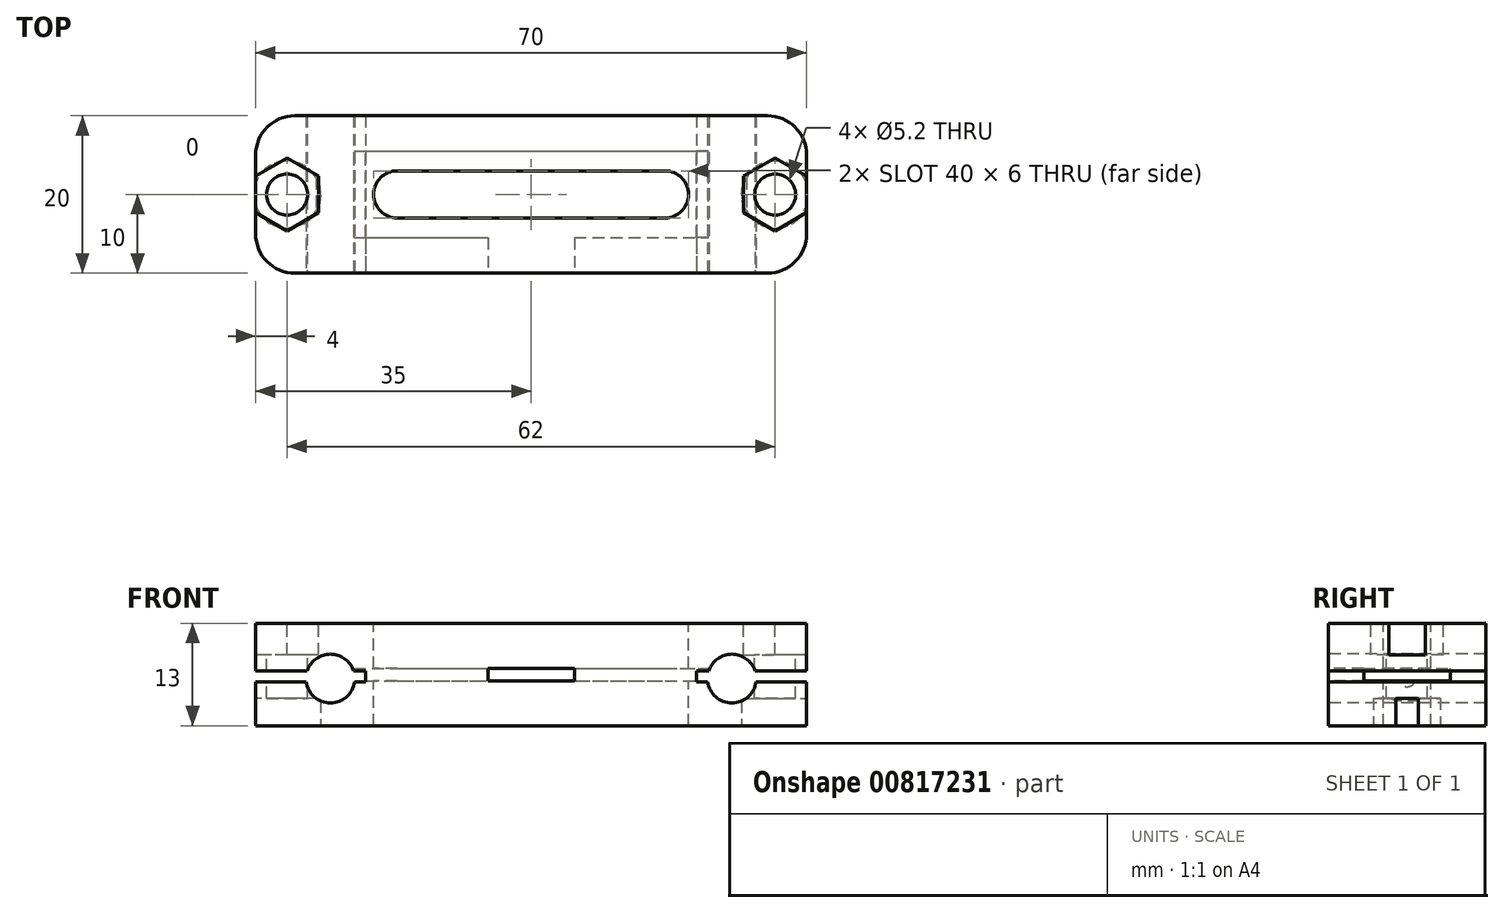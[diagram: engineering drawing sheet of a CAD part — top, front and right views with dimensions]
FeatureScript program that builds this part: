
annotation { "Feature Type Name" : "Feature", "Feature Type Description" : "" }
export const myFeature = defineFeature(function(context is Context, id is Id, definition is map)
    precondition{}
    {
        {
            var Q0;
            Q0=qCreatedBy(makeId("Top.planeOp"),FACE);
            var sketch = newSketch(context, id + "F0", { "sketchPlane" : qUnion([Q0])});
            skLineSegment(sketch, "E0.bottom", {"start": v(35, -10) * mm, "end": v(-35, -10) * mm});
            skLineSegment(sketch, "E0.top", {"start": v(35, 10) * mm, "end": v(-35, 10) * mm});
            skLineSegment(sketch, "E0.left", {"start": v(35, -10) * mm, "end": v(35, 10) * mm});
            skLineSegment(sketch, "E0.right", {"start": v(-35, -10) * mm, "end": v(-35, 10) * mm});
            skPoint(sketch, "E0.middle", {"position": v(0, 0) * mm});
            skSolve(sketch);
        }
        {
            var Q0;
            Q0 = qSketchRegion(id + "F0", true);
            extrude(context, id + "F1", {"entities" : qUnion([Q0]), "endBound" : BoundingType.SYMMETRIC, "depth" : 13 * mm, "offsetDistance" : 25 * mm});
        }
        {
            var Q0;
            Q0=makeQuery(id+"F1.opExtrude","CAP_FACE",FACE,{"disambiguationData":[OSD([sQuery(id+"F0.wireOp",EDGE,"E0.bottom"),sQuery(id+"F0.wireOp",EDGE,"E0.top"),sQuery(id+"F0.wireOp",EDGE,"E0.left"),sQuery(id+"F0.wireOp",EDGE,"E0.right")])],"isStart":false});
            var sketch = newSketch(context, id + "F2", { "sketchPlane" : qUnion([Q0])});
            skLineSegment(sketch, "E1.bottom", {"start": v(17, -3) * mm, "end": v(-17, -3) * mm});
            skLineSegment(sketch, "E1.top", {"start": v(17, 3) * mm, "end": v(-17, 3) * mm});
            skPoint(sketch, "E1.middle", {"position": v(0, 0) * mm});
            skArc(sketch, "E2", {"start": v(-17, 3) * mm, "mid": v(-20, 0) * mm, "end": v(-17, -3) * mm});
            skArc(sketch, "E3", {"start": v(17, 3) * mm, "mid": v(20, 0) * mm, "end": v(17, -3) * mm});
            skSolve(sketch);
        }
        {
            var Q0;
            Q0=makeQuery(id+"F2.imprint","IMPRINT",FACE,{"disambiguationData":[TD([[makeQuery(id+"F2.imprint","IMPRINT",EDGE,{"derivedFrom":sQuery(id+"F2.wireOp",EDGE,"E1.bottom")}),1.0]])]});
            var sketch = newSketch(context, id + "F3", { "sketchPlane" : qUnion([Q0])});
            skCircle(sketch, "E4.cCircle", {"center": v(-31, 0) * mm, "radius": 4 * mm, "construction": true});
            skLineSegment(sketch, "E4.0", {"start": v(-27, -2.3) * mm, "end": v(-31, -4.62) * mm});
            skLineSegment(sketch, "E4.1", {"start": v(-31, -4.62) * mm, "end": v(-35, -2.3) * mm});
            skLineSegment(sketch, "E4.2", {"start": v(-35, -2.3) * mm, "end": v(-35, 2.3) * mm});
            skLineSegment(sketch, "E4.3", {"start": v(-35, 2.3) * mm, "end": v(-31, 4.62) * mm});
            skLineSegment(sketch, "E4.4", {"start": v(-31, 4.62) * mm, "end": v(-27, 2.3) * mm});
            skLineSegment(sketch, "E4.5", {"start": v(-27, 2.3) * mm, "end": v(-27, -2.3) * mm});
            skPoint(sketch, "E4.0.midPoint", {"position": v(-29, -3.46) * mm});
            skCircle(sketch, "E5.cCircle", {"center": v(31, 0) * mm, "radius": 4 * mm, "construction": true});
            skLineSegment(sketch, "E5.0", {"start": v(35, 2.3) * mm, "end": v(35, -2.3) * mm});
            skLineSegment(sketch, "E5.1", {"start": v(35, -2.3) * mm, "end": v(31, -4.62) * mm});
            skLineSegment(sketch, "E5.2", {"start": v(31, -4.62) * mm, "end": v(27, -2.3) * mm});
            skLineSegment(sketch, "E5.3", {"start": v(27, -2.3) * mm, "end": v(27, 2.3) * mm});
            skLineSegment(sketch, "E5.4", {"start": v(27, 2.3) * mm, "end": v(31, 4.62) * mm});
            skLineSegment(sketch, "E5.5", {"start": v(31, 4.62) * mm, "end": v(35, 2.3) * mm});
            skPoint(sketch, "E5.0.midPoint", {"position": v(35, 0) * mm});
            skSolve(sketch);
        }
        {
            var Q0;
            Q0 = qSketchRegion(id + "F3", true);
            extrude(context, id + "F4", {"entities" : qUnion([Q0]), "operationType" : NewBodyOperationType.REMOVE, "oppositeDirection" : true, "depth" : 4 * mm, "offsetDistance" : 25 * mm});
        }
        {
            var Q0;
            Q0=makeQuery(id+"F2.imprint","IMPRINT",FACE,{"disambiguationData":[TD([[makeQuery(id+"F2.imprint","IMPRINT",EDGE,{"derivedFrom":sQuery(id+"F2.wireOp",EDGE,"E1.bottom")}),1.0]])]});
            var sketch = newSketch(context, id + "F5", { "sketchPlane" : qUnion([Q0])});
            skCircle(sketch, "E6", {"center": v(-31, 0) * mm, "radius": 2.6 * mm});
            skCircle(sketch, "E7", {"center": v(31, 0) * mm, "radius": 2.6 * mm});
            skSolve(sketch);
        }
        {
            var Q0;
            Q0 = qSketchRegion(id + "F5", true);
            extrude(context, id + "F6", {"entities" : qUnion([Q0]), "operationType" : NewBodyOperationType.REMOVE, "endBound" : BoundingType.THROUGH_ALL, "oppositeDirection" : true, "depth" : 25 * mm, "offsetDistance" : 25 * mm});
        }
        {
            var Q0;
            Q0 = qSketchRegion(id + "F2", true);
            extrude(context, id + "F7", {"entities" : qUnion([Q0]), "operationType" : NewBodyOperationType.REMOVE, "endBound" : BoundingType.THROUGH_ALL, "oppositeDirection" : true, "depth" : 25 * mm, "offsetDistance" : 25 * mm});
        }
        {
            var Q0;
            Q0=makeQuery(id+"F1.opExtrude","SWEPT_FACE",FACE,{"disambiguationData":[OSD([sQuery(id+"F0.wireOp",EDGE,"E0.bottom")])]});
            var sketch = newSketch(context, id + "F8", { "sketchPlane" : qUnion([Q0])});
            skCircle(sketch, "E8", {"center": v(-25.5, -0.5) * mm, "radius": 3.1 * mm});
            skCircle(sketch, "E9", {"center": v(25.5, -0.5) * mm, "radius": 3.1 * mm});
            skSolve(sketch);
        }
        {
            var Q0;
            Q0=makeQuery(id+"FGKyORt9fG3GxLQ_1.opExtrude","CAP_EDGE",EDGE,{"disambiguationData":[OSD([sQuery(id+"FUYUVBWRlq5jCbc_1.wireOp",EDGE,"ZpnfMVQ8-PDP1-Nz7W-Utch-BhDVuRkNCdpB.left")])],"isStart":false});
            var Q1;
            {var subQ0=sQuery(id+"F0.wireOp",EDGE,"E0.left");var subQ1=sQuery(id+"F0.wireOp",EDGE,"E0.top");Q1=makeQuery(id+"F16.boolean.opBoolean","SPLIT",EDGE,{"disambiguationData":[TD([makeQuery(id+"F16.opExtrude","SWEPT_FACE",FACE,{"disambiguationData":[OSD([sQuery(id+"F15.wireOp",EDGE,"E13.top")])]})])],"derivedFrom":makeQuery(id+"F1.opExtrude","SWEPT_EDGE",EDGE,{"disambiguationData":[OSD([subQ1,subQ0])]})});}
            var Q2;
            {var subQ0=sQuery(id+"F0.wireOp",EDGE,"E0.left");var subQ1=sQuery(id+"F0.wireOp",EDGE,"E0.top");Q2=makeQuery(id+"F16.boolean.opBoolean","SPLIT",EDGE,{"disambiguationData":[TD([makeQuery(id+"F16.opExtrude","SWEPT_FACE",FACE,{"disambiguationData":[OSD([sQuery(id+"F15.wireOp",EDGE,"E13.bottom")])]})])],"derivedFrom":makeQuery(id+"F1.opExtrude","SWEPT_EDGE",EDGE,{"disambiguationData":[OSD([subQ1,subQ0])]})});}
            var Q3;
            {var subQ0=sQuery(id+"F0.wireOp",EDGE,"E0.bottom");var subQ1=sQuery(id+"F0.wireOp",EDGE,"E0.left");Q3=makeQuery(id+"F16.boolean.opBoolean","SPLIT",EDGE,{"disambiguationData":[TD([makeQuery(id+"F16.opExtrude","SWEPT_FACE",FACE,{"disambiguationData":[OSD([sQuery(id+"F15.wireOp",EDGE,"E13.top")])]})])],"derivedFrom":makeQuery(id+"F1.opExtrude","SWEPT_EDGE",EDGE,{"disambiguationData":[OSD([subQ0,subQ1])]})});}
            var Q4;
            {var subQ0=sQuery(id+"F0.wireOp",EDGE,"E0.bottom");var subQ1=sQuery(id+"F0.wireOp",EDGE,"E0.left");Q4=makeQuery(id+"F16.boolean.opBoolean","SPLIT",EDGE,{"disambiguationData":[TD([makeQuery(id+"F16.opExtrude","SWEPT_FACE",FACE,{"disambiguationData":[OSD([sQuery(id+"F15.wireOp",EDGE,"E13.bottom")])]})])],"derivedFrom":makeQuery(id+"F1.opExtrude","SWEPT_EDGE",EDGE,{"disambiguationData":[OSD([subQ0,subQ1])]})});}
            var Q5;
            {var subQ0=sQuery(id+"F0.wireOp",EDGE,"E0.bottom");var subQ1=sQuery(id+"F0.wireOp",EDGE,"E0.right");Q5=makeQuery(id+"F16.boolean.opBoolean","SPLIT",EDGE,{"disambiguationData":[TD([makeQuery(id+"F16.opExtrude","SWEPT_FACE",FACE,{"disambiguationData":[OSD([sQuery(id+"F15.wireOp",EDGE,"E12.bottom")])]})])],"derivedFrom":makeQuery(id+"F1.opExtrude","SWEPT_EDGE",EDGE,{"disambiguationData":[OSD([subQ0,subQ1])]})});}
            var Q6;
            {var subQ0=sQuery(id+"F0.wireOp",EDGE,"E0.bottom");var subQ1=sQuery(id+"F0.wireOp",EDGE,"E0.right");Q6=makeQuery(id+"F16.boolean.opBoolean","SPLIT",EDGE,{"disambiguationData":[TD([makeQuery(id+"F16.opExtrude","SWEPT_FACE",FACE,{"disambiguationData":[OSD([sQuery(id+"F15.wireOp",EDGE,"E12.top")])]})])],"derivedFrom":makeQuery(id+"F1.opExtrude","SWEPT_EDGE",EDGE,{"disambiguationData":[OSD([subQ0,subQ1])]})});}
            var Q7;
            {var subQ0=sQuery(id+"F0.wireOp",EDGE,"E0.right");var subQ1=sQuery(id+"F0.wireOp",EDGE,"E0.top");Q7=makeQuery(id+"F16.boolean.opBoolean","SPLIT",EDGE,{"disambiguationData":[TD([makeQuery(id+"F16.opExtrude","SWEPT_FACE",FACE,{"disambiguationData":[OSD([sQuery(id+"F15.wireOp",EDGE,"E12.top")])]})])],"derivedFrom":makeQuery(id+"F1.opExtrude","SWEPT_EDGE",EDGE,{"disambiguationData":[OSD([subQ1,subQ0])]})});}
            var Q8;
            {var subQ0=sQuery(id+"F0.wireOp",EDGE,"E0.right");var subQ1=sQuery(id+"F0.wireOp",EDGE,"E0.top");Q8=makeQuery(id+"F16.boolean.opBoolean","SPLIT",EDGE,{"disambiguationData":[TD([makeQuery(id+"F16.opExtrude","SWEPT_FACE",FACE,{"disambiguationData":[OSD([sQuery(id+"F15.wireOp",EDGE,"E12.bottom")])]})])],"derivedFrom":makeQuery(id+"F1.opExtrude","SWEPT_EDGE",EDGE,{"disambiguationData":[OSD([subQ1,subQ0])]})});}
            var Q9;
            Q9=makeQuery(id+"FGKyORt9fG3GxLQ_1.opExtrude","CAP_EDGE",EDGE,{"disambiguationData":[OSD([sQuery(id+"FUYUVBWRlq5jCbc_1.wireOp",EDGE,"ZpnfMVQ8-PDP1-Nz7W-Utch-BhDVuRkNCdpB.right")])],"isStart":false});
            fillet(context, id + "F9", {"entities" : qUnion([Q0, Q1, Q2, Q3, Q4, Q5, Q6, Q7, Q8, Q9]), "radius" : 5 * mm, "tangentPropagation" : true, "allowEdgeOverflow" : false});
        }
        {
            var Q0;
            Q0 = qSketchRegion(id + "F8", true);
            extrude(context, id + "F10", {"entities" : qUnion([Q0]), "operationType" : NewBodyOperationType.REMOVE, "endBound" : BoundingType.THROUGH_ALL, "oppositeDirection" : true, "depth" : 25 * mm, "offsetDistance" : 25 * mm});
        }
        {
            var Q0;
            Q0=qCreatedBy(makeId("Top.planeOp"),FACE);
            var sketch = newSketch(context, id + "F11", { "sketchPlane" : qUnion([Q0])});
            skLineSegment(sketch, "E10.bottom", {"start": v(-22.5, -5.5) * mm, "end": v(22.5, -5.5) * mm});
            skLineSegment(sketch, "E10.top", {"start": v(-22.5, 5.5) * mm, "end": v(22.5, 5.5) * mm});
            skLineSegment(sketch, "E10.left", {"start": v(-22.5, -5.5) * mm, "end": v(-22.5, 5.5) * mm});
            skLineSegment(sketch, "E10.right", {"start": v(22.5, -5.5) * mm, "end": v(22.5, 5.5) * mm});
            skPoint(sketch, "E10.middle", {"position": v(0, 0) * mm});
            skSolve(sketch);
        }
        {
            var Q0;
            Q0 = qSketchRegion(id + "F11", true);
            extrude(context, id + "F12", {"entities" : qUnion([Q0]), "operationType" : NewBodyOperationType.REMOVE, "endBound" : BoundingType.SYMMETRIC, "oppositeDirection" : true, "depth" : 1.6 * mm, "offsetDistance" : 25 * mm});
        }
        {
            var Q0;
            Q0=makeQuery(id+"F1.opExtrude","SWEPT_FACE",FACE,{"disambiguationData":[OSD([sQuery(id+"F0.wireOp",EDGE,"E0.bottom")])]});
            var sketch = newSketch(context, id + "F13", { "sketchPlane" : qUnion([Q0])});
            skLineSegment(sketch, "E11.bottom", {"start": v(5.5, -0.8) * mm, "end": v(-5.5, -0.8) * mm});
            skLineSegment(sketch, "E11.top", {"start": v(5.5, 0.8) * mm, "end": v(-5.5, 0.8) * mm});
            skLineSegment(sketch, "E11.left", {"start": v(5.5, -0.8) * mm, "end": v(5.5, 0.8) * mm});
            skLineSegment(sketch, "E11.right", {"start": v(-5.5, -0.8) * mm, "end": v(-5.5, 0.8) * mm});
            skPoint(sketch, "E11.middle", {"position": v(0, 0) * mm});
            skSolve(sketch);
        }
        {
            var Q0;
            Q0 = qSketchRegion(id + "F13", true);
            extrude(context, id + "F14", {"entities" : qUnion([Q0]), "operationType" : NewBodyOperationType.REMOVE, "endBound" : BoundingType.UP_TO_NEXT, "oppositeDirection" : true, "depth" : 25 * mm, "offsetDistance" : 25 * mm});
        }
        {
            var Q0;
            Q0=makeQuery(id+"F1.opExtrude","SWEPT_FACE",FACE,{"disambiguationData":[OSD([sQuery(id+"F0.wireOp",EDGE,"E0.bottom")])]});
            var sketch = newSketch(context, id + "F15", { "sketchPlane" : qUnion([Q0])});
            skLineSegment(sketch, "E12.bottom", {"start": v(-35, -0.9) * mm, "end": v(-21, -0.9) * mm});
            skLineSegment(sketch, "E12.top", {"start": v(-35, 0.5) * mm, "end": v(-21, 0.5) * mm});
            skLineSegment(sketch, "E12.left", {"start": v(-35, -0.9) * mm, "end": v(-35, 0.5) * mm});
            skLineSegment(sketch, "E12.right", {"start": v(-21, -0.9) * mm, "end": v(-21, 0.5) * mm});
            skLineSegment(sketch, "E13.bottom", {"start": v(35, -0.9) * mm, "end": v(21, -0.9) * mm});
            skLineSegment(sketch, "E13.top", {"start": v(35, 0.5) * mm, "end": v(21, 0.5) * mm});
            skLineSegment(sketch, "E13.left", {"start": v(35, -0.9) * mm, "end": v(35, 0.5) * mm});
            skLineSegment(sketch, "E13.right", {"start": v(21, -0.9) * mm, "end": v(21, 0.5) * mm});
            skSolve(sketch);
        }
        {
            var Q0;
            Q0 = qSketchRegion(id + "F15", true);
            extrude(context, id + "F16", {"entities" : qUnion([Q0]), "operationType" : NewBodyOperationType.REMOVE, "endBound" : BoundingType.THROUGH_ALL, "oppositeDirection" : true, "depth" : 25 * mm, "offsetDistance" : 25 * mm});
        }
        {
            var Q0;
            Q0=makeQuery(id+"F1.opExtrude","CAP_FACE",FACE,{"disambiguationData":[OSD([sQuery(id+"F0.wireOp",EDGE,"E0.bottom"),sQuery(id+"F0.wireOp",EDGE,"E0.top"),sQuery(id+"F0.wireOp",EDGE,"E0.left"),sQuery(id+"F0.wireOp",EDGE,"E0.right")])],"isStart":true});
            var sketch = newSketch(context, id + "F17", { "sketchPlane" : qUnion([Q0])});
            skCircle(sketch, "E14", {"center": v(31, 0) * mm, "radius": 4.25 * mm});
            skCircle(sketch, "E15", {"center": v(-31, 0) * mm, "radius": 4.25 * mm});
            skSolve(sketch);
        }
        {
            var Q0;
            Q0 = qSketchRegion(id + "F17", true);
            extrude(context, id + "F18", {"entities" : qUnion([Q0]), "operationType" : NewBodyOperationType.REMOVE, "oppositeDirection" : true, "depth" : 3.5 * mm, "offsetDistance" : 25 * mm});
        }
    });
